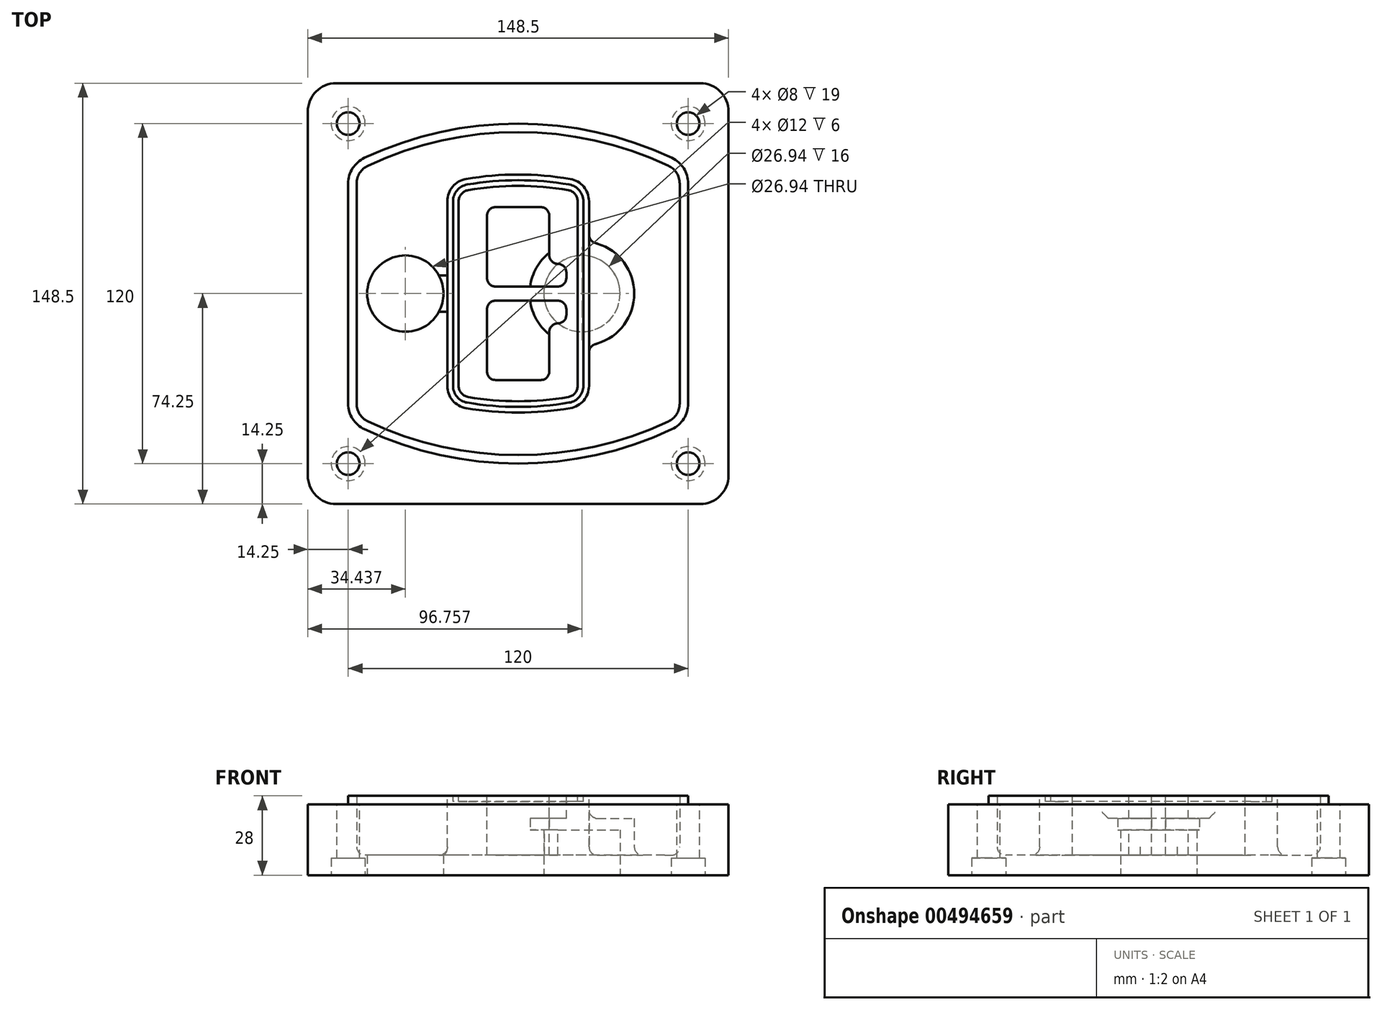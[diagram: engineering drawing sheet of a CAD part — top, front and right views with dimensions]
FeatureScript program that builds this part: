
annotation { "Feature Type Name" : "Feature", "Feature Type Description" : "" }
export const myFeature = defineFeature(function(context is Context, id is Id, definition is map)
    precondition{}
    {
        {
            var Q0;
            Q0=qCreatedBy(makeId("Top.planeOp"),FACE);
            var sketch = newSketch(context, id + "F0", { "sketchPlane" : qUnion([Q0])});
            skPoint(sketch, "E0.rect.middle", {"position": v(0, 0) * mm});
            skLineSegment(sketch, "E1.bottom", {"start": v(-64.25, -74.25) * mm, "end": v(64.25, -74.25) * mm});
            skLineSegment(sketch, "E1.top", {"start": v(-64.25, 74.25) * mm, "end": v(64.25, 74.25) * mm});
            skLineSegment(sketch, "E1.left", {"start": v(-74.25, -64.25) * mm, "end": v(-74.25, 64.25) * mm});
            skLineSegment(sketch, "E1.right", {"start": v(74.25, -64.25) * mm, "end": v(74.25, 64.25) * mm});
            skLineSegment(sketch, "E2", {"start": v(-74.25, 74.25) * mm, "end": v(74.25, -74.25) * mm, "construction": true});
            skLineSegment(sketch, "E3", {"start": v(74.25, 74.25) * mm, "end": v(-74.25, -74.25) * mm, "construction": true});
            skCircle(sketch, "E4", {"center": v(-60, 60) * mm, "radius": 4 * mm});
            skCircle(sketch, "E5", {"center": v(60, 60) * mm, "radius": 4 * mm});
            skCircle(sketch, "E6", {"center": v(60, -60) * mm, "radius": 4 * mm});
            skCircle(sketch, "E7", {"center": v(-60, -60) * mm, "radius": 4 * mm});
            skLineSegment(sketch, "E8", {"start": v(-60, 60) * mm, "end": v(60, 60) * mm, "construction": true});
            skLineSegment(sketch, "E9", {"start": v(60, 60) * mm, "end": v(60, -60) * mm, "construction": true});
            skLineSegment(sketch, "E10", {"start": v(60, -60) * mm, "end": v(-60, -60) * mm, "construction": true});
            skLineSegment(sketch, "E11", {"start": v(-60, -60) * mm, "end": v(-60, 60) * mm, "construction": true});
            skLineSegment(sketch, "E12", {"start": v(-60, 38.83) * mm, "end": v(-60, -38.83) * mm});
            skLineSegment(sketch, "E13", {"start": v(60, 38.83) * mm, "end": v(60, -38.83) * mm});
            skArc(sketch, "E14", {"start": v(54.26, 47.88) * mm, "mid": v(0, 60) * mm, "end": v(-54.26, 47.88) * mm});
            skArc(sketch, "E15", {"start": v(-54.26, -47.88) * mm, "mid": v(0, -60) * mm, "end": v(54.26, -47.88) * mm});
            skLineSegment(sketch, "E16", {"start": v(-60, 0) * mm, "end": v(60, 0) * mm, "construction": true});
            skPoint(sketch, "E17.visualSharp", {"position": v(-60, -45) * mm});
            skArc(sketch, "E17.filletArc", {"start": v(-60, -38.83) * mm, "mid": v(-58.44, -44.2) * mm, "end": v(-54.26, -47.88) * mm});
            skPoint(sketch, "E18.visualSharp", {"position": v(-60, 45) * mm});
            skArc(sketch, "E18.filletArc", {"start": v(-54.26, 47.88) * mm, "mid": v(-58.44, 44.2) * mm, "end": v(-60, 38.83) * mm});
            skPoint(sketch, "E19.visualSharp", {"position": v(60, 45) * mm});
            skArc(sketch, "E19.filletArc", {"start": v(60, 38.83) * mm, "mid": v(58.44, 44.2) * mm, "end": v(54.26, 47.88) * mm});
            skPoint(sketch, "E20.visualSharp", {"position": v(60, -45) * mm});
            skArc(sketch, "E20.filletArc", {"start": v(54.26, -47.88) * mm, "mid": v(58.44, -44.2) * mm, "end": v(60, -38.83) * mm});
            skPoint(sketch, "E21.visualSharp", {"position": v(-74.25, 74.25) * mm});
            skArc(sketch, "E21.filletArc", {"start": v(-64.25, 74.25) * mm, "mid": v(-71.32, 71.32) * mm, "end": v(-74.25, 64.25) * mm});
            skPoint(sketch, "E22.visualSharp", {"position": v(74.25, 74.25) * mm});
            skArc(sketch, "E22.filletArc", {"start": v(74.25, 64.25) * mm, "mid": v(71.32, 71.32) * mm, "end": v(64.25, 74.25) * mm});
            skPoint(sketch, "E23.visualSharp", {"position": v(74.25, -74.25) * mm});
            skArc(sketch, "E23.filletArc", {"start": v(64.25, -74.25) * mm, "mid": v(71.32, -71.32) * mm, "end": v(74.25, -64.25) * mm});
            skPoint(sketch, "E24.visualSharp", {"position": v(-74.25, -74.25) * mm});
            skArc(sketch, "E24.filletArc", {"start": v(-74.25, -64.25) * mm, "mid": v(-71.32, -71.32) * mm, "end": v(-64.25, -74.25) * mm});
            skArc(sketch, "E25.0", {"start": v(57, 38.83) * mm, "mid": v(55.9, 42.58) * mm, "end": v(52.98, 45.17) * mm});
            skLineSegment(sketch, "E25.1", {"start": v(57, 38.83) * mm, "end": v(57, -38.83) * mm});
            skArc(sketch, "E25.2", {"start": v(52.98, -45.17) * mm, "mid": v(55.9, -42.58) * mm, "end": v(57, -38.83) * mm});
            skArc(sketch, "E25.3", {"start": v(-52.98, -45.17) * mm, "mid": v(0, -57) * mm, "end": v(52.98, -45.17) * mm});
            skArc(sketch, "E25.4", {"start": v(-57, -38.83) * mm, "mid": v(-55.9, -42.58) * mm, "end": v(-52.98, -45.17) * mm});
            skArc(sketch, "E25.5", {"start": v(52.98, 45.17) * mm, "mid": v(0, 57) * mm, "end": v(-52.98, 45.17) * mm});
            skLineSegment(sketch, "E25.6", {"start": v(-57, 38.83) * mm, "end": v(-57, -38.83) * mm});
            skArc(sketch, "E25.7", {"start": v(-52.98, 45.17) * mm, "mid": v(-55.9, 42.58) * mm, "end": v(-57, 38.83) * mm});
            skArc(sketch, "E26.0", {"start": v(-55.96, 51.5) * mm, "mid": v(-61.82, 46.33) * mm, "end": v(-64, 38.83) * mm});
            skArc(sketch, "E26.1", {"start": v(55.96, 51.5) * mm, "mid": v(0, 64) * mm, "end": v(-55.96, 51.5) * mm});
            skArc(sketch, "E26.2", {"start": v(64, 38.83) * mm, "mid": v(61.82, 46.33) * mm, "end": v(55.96, 51.5) * mm});
            skLineSegment(sketch, "E26.3", {"start": v(64, 38.83) * mm, "end": v(64, -38.83) * mm});
            skArc(sketch, "E26.4", {"start": v(55.96, -51.5) * mm, "mid": v(61.82, -46.33) * mm, "end": v(64, -38.83) * mm});
            skLineSegment(sketch, "E26.5", {"start": v(-64, 38.83) * mm, "end": v(-64, -38.83) * mm});
            skArc(sketch, "E26.6", {"start": v(-55.96, -51.5) * mm, "mid": v(0, -64) * mm, "end": v(55.96, -51.5) * mm});
            skArc(sketch, "E26.7", {"start": v(-64, -38.83) * mm, "mid": v(-61.82, -46.33) * mm, "end": v(-55.96, -51.5) * mm});
            skSolve(sketch);
        }
        {
            var Q0;
            Q0=makeQuery(id+"F0.imprint","IMPRINT",FACE,{"disambiguationData":[TD([[makeQuery(id+"F0.imprint","IMPRINT",EDGE,{"derivedFrom":sQuery(id+"F0.wireOp",EDGE,"E1.bottom")}),1.0]])]});
            var Q1;
            Q1=makeQuery(id+"F0.imprint","IMPRINT",FACE,{"disambiguationData":[TD([[makeQuery(id+"F0.imprint","IMPRINT",EDGE,{"derivedFrom":sQuery(id+"F0.wireOp",EDGE,"E12")}),1.0]])]});
            var Q2;
            Q2=makeQuery(id+"F0.imprint","IMPRINT",FACE,{"disambiguationData":[TD([[makeQuery(id+"F0.imprint","IMPRINT",EDGE,{"derivedFrom":sQuery(id+"F0.wireOp",EDGE,"E25.0")}),1.0]])]});
            var Q3;
            Q3=makeQuery(id+"F0.imprint","IMPRINT",FACE,{"disambiguationData":[TD([[makeQuery(id+"F0.imprint","IMPRINT",EDGE,{"derivedFrom":sQuery(id+"F0.wireOp",EDGE,"E12")}),-1.0]])]});
            extrude(context, id + "F1", {"entities" : qUnion([Q0, Q1, Q2, Q3]), "oppositeDirection" : true, "depth" : 25 * mm});
        }
        {
            var Q0;
            Q0=makeQuery(id+"F0.imprint","IMPRINT",FACE,{"disambiguationData":[TD([[makeQuery(id+"F0.imprint","IMPRINT",EDGE,{"derivedFrom":sQuery(id+"F0.wireOp",EDGE,"E12")}),1.0]])]});
            extrude(context, id + "F2", {"entities" : qUnion([Q0]), "operationType" : NewBodyOperationType.ADD, "depth" : 3 * mm});
        }
        {
            var Q0;
            Q0=makeQuery(id+"F0.imprint","IMPRINT",FACE,{"disambiguationData":[TD([[makeQuery(id+"F0.imprint","IMPRINT",EDGE,{"derivedFrom":sQuery(id+"F0.wireOp",EDGE,"E25.0")}),1.0]])]});
            extrude(context, id + "F3", {"entities" : qUnion([Q0]), "operationType" : NewBodyOperationType.REMOVE, "oppositeDirection" : true, "depth" : 18 * mm});
        }
        {
            var Q0;
            Q0=makeQuery(id+"F2.opExtrude","CAP_FACE",FACE,{"disambiguationData":[OSD([sQuery(id+"F0.wireOp",EDGE,"E12"),sQuery(id+"F0.wireOp",EDGE,"E13"),sQuery(id+"F0.wireOp",EDGE,"E14"),sQuery(id+"F0.wireOp",EDGE,"E15"),sQuery(id+"F0.wireOp",EDGE,"E17.filletArc"),sQuery(id+"F0.wireOp",EDGE,"E18.filletArc"),sQuery(id+"F0.wireOp",EDGE,"E19.filletArc"),sQuery(id+"F0.wireOp",EDGE,"E20.filletArc"),sQuery(id+"F0.wireOp",EDGE,"E25.0"),sQuery(id+"F0.wireOp",EDGE,"E25.1"),sQuery(id+"F0.wireOp",EDGE,"E25.2"),sQuery(id+"F0.wireOp",EDGE,"E25.3"),sQuery(id+"F0.wireOp",EDGE,"E25.4"),sQuery(id+"F0.wireOp",EDGE,"E25.5"),sQuery(id+"F0.wireOp",EDGE,"E25.6"),sQuery(id+"F0.wireOp",EDGE,"E25.7")])],"isStart":false});
            var sketch = newSketch(context, id + "F4", { "sketchPlane" : qUnion([Q0])});
            skArc(sketch, "E27.0", {"start": v(-18.34, -40.45) * mm, "mid": v(0, -42) * mm, "end": v(18.34, -40.45) * mm});
            skArc(sketch, "E28.0", {"start": v(18.34, 40.45) * mm, "mid": v(0, 42) * mm, "end": v(-18.34, 40.45) * mm});
            skLineSegment(sketch, "E29", {"start": v(-25, 32.57) * mm, "end": v(-25, -32.57) * mm});
            skLineSegment(sketch, "E30", {"start": v(25, 32.57) * mm, "end": v(25, -32.57) * mm});
            skLineSegment(sketch, "E31", {"start": v(-25, 39.1) * mm, "end": v(25, 39.1) * mm, "construction": true});
            skLineSegment(sketch, "E32", {"start": v(-25, -39.1) * mm, "end": v(25, -39.1) * mm, "construction": true});
            skPoint(sketch, "E33.visualSharp", {"position": v(-25, 39.1) * mm});
            skArc(sketch, "E33.filletArc", {"start": v(-18.34, 40.45) * mm, "mid": v(-23.11, 37.73) * mm, "end": v(-25, 32.57) * mm});
            skPoint(sketch, "E34.visualSharp", {"position": v(25, 39.1) * mm});
            skArc(sketch, "E34.filletArc", {"start": v(25, 32.57) * mm, "mid": v(23.11, 37.73) * mm, "end": v(18.34, 40.45) * mm});
            skPoint(sketch, "E35.visualSharp", {"position": v(25, -39.1) * mm});
            skArc(sketch, "E35.filletArc", {"start": v(18.34, -40.45) * mm, "mid": v(23.11, -37.73) * mm, "end": v(25, -32.57) * mm});
            skPoint(sketch, "E36.visualSharp", {"position": v(-25, -39.1) * mm});
            skArc(sketch, "E36.filletArc", {"start": v(-25, -32.57) * mm, "mid": v(-23.11, -37.73) * mm, "end": v(-18.34, -40.45) * mm});
            skArc(sketch, "E37.0", {"start": v(52.98, 45.17) * mm, "mid": v(0, 57) * mm, "end": v(-52.98, 45.17) * mm});
            skArc(sketch, "E37.1", {"start": v(-52.98, 45.17) * mm, "mid": v(-55.9, 42.58) * mm, "end": v(-57, 38.83) * mm});
            skLineSegment(sketch, "E37.2", {"start": v(-57, 38.83) * mm, "end": v(-57, -38.83) * mm});
            skArc(sketch, "E37.3", {"start": v(-57, -38.83) * mm, "mid": v(-55.9, -42.58) * mm, "end": v(-52.98, -45.17) * mm});
            skArc(sketch, "E37.4", {"start": v(-52.98, -45.17) * mm, "mid": v(0, -57) * mm, "end": v(52.98, -45.17) * mm});
            skArc(sketch, "E37.5", {"start": v(52.98, -45.17) * mm, "mid": v(55.9, -42.58) * mm, "end": v(57, -38.83) * mm});
            skLineSegment(sketch, "E37.6", {"start": v(57, 38.83) * mm, "end": v(57, -38.83) * mm});
            skArc(sketch, "E37.7", {"start": v(57, 38.83) * mm, "mid": v(55.9, 42.58) * mm, "end": v(52.98, 45.17) * mm});
            skLineSegment(sketch, "E38.0", {"start": v(23, 32.57) * mm, "end": v(23, -32.57) * mm});
            skArc(sketch, "E38.1", {"start": v(18, -38.48) * mm, "mid": v(21.58, -36.44) * mm, "end": v(23, -32.57) * mm});
            skArc(sketch, "E38.2", {"start": v(-18, -38.48) * mm, "mid": v(0, -40) * mm, "end": v(18, -38.48) * mm});
            skArc(sketch, "E38.3", {"start": v(-23, -32.57) * mm, "mid": v(-21.58, -36.44) * mm, "end": v(-18, -38.48) * mm});
            skLineSegment(sketch, "E38.4", {"start": v(-23, 32.57) * mm, "end": v(-23, -32.57) * mm});
            skArc(sketch, "E38.5", {"start": v(23, 32.57) * mm, "mid": v(21.58, 36.44) * mm, "end": v(18, 38.48) * mm});
            skArc(sketch, "E38.6", {"start": v(-18, 38.48) * mm, "mid": v(-21.58, 36.44) * mm, "end": v(-23, 32.57) * mm});
            skArc(sketch, "E38.7", {"start": v(18, 38.48) * mm, "mid": v(0, 40) * mm, "end": v(-18, 38.48) * mm});
            skArc(sketch, "E39.0", {"start": v(21, 32.57) * mm, "mid": v(20.06, 35.15) * mm, "end": v(17.67, 36.5) * mm});
            skLineSegment(sketch, "E39.1", {"start": v(21, 32.57) * mm, "end": v(21, -32.57) * mm});
            skArc(sketch, "E39.2", {"start": v(17.67, -36.5) * mm, "mid": v(20.06, -35.15) * mm, "end": v(21, -32.57) * mm});
            skArc(sketch, "E39.3", {"start": v(-17.67, -36.5) * mm, "mid": v(0, -38) * mm, "end": v(17.67, -36.5) * mm});
            skArc(sketch, "E39.4", {"start": v(-21, -32.57) * mm, "mid": v(-20.06, -35.15) * mm, "end": v(-17.67, -36.5) * mm});
            skArc(sketch, "E39.5", {"start": v(17.67, 36.5) * mm, "mid": v(0, 38) * mm, "end": v(-17.67, 36.5) * mm});
            skLineSegment(sketch, "E39.6", {"start": v(-21, 32.57) * mm, "end": v(-21, -32.57) * mm});
            skArc(sketch, "E39.7", {"start": v(-17.67, 36.5) * mm, "mid": v(-20.06, 35.15) * mm, "end": v(-21, 32.57) * mm});
            skLineSegment(sketch, "E40", {"start": v(-25, 0) * mm, "end": v(25, 0) * mm, "construction": true});
            skLineSegment(sketch, "E41", {"start": v(-11, 5.5) * mm, "end": v(-11, 27.5) * mm});
            skLineSegment(sketch, "E42", {"start": v(-8, 30.5) * mm, "end": v(8, 30.5) * mm});
            skLineSegment(sketch, "E43", {"start": v(11, 27.5) * mm, "end": v(11, 13.5) * mm});
            skLineSegment(sketch, "E44", {"start": v(14, 10.5) * mm, "end": v(14, 10.5) * mm});
            skLineSegment(sketch, "E45", {"start": v(17, 7.5) * mm, "end": v(17, 5.5) * mm});
            skLineSegment(sketch, "E46", {"start": v(14, 2.5) * mm, "end": v(-8, 2.5) * mm});
            skPoint(sketch, "E47.visualSharp", {"position": v(-11, 30.5) * mm});
            skArc(sketch, "E47.filletArc", {"start": v(-8, 30.5) * mm, "mid": v(-10.12, 29.62) * mm, "end": v(-11, 27.5) * mm});
            skPoint(sketch, "E48.visualSharp", {"position": v(11, 30.5) * mm});
            skArc(sketch, "E48.filletArc", {"start": v(11, 27.5) * mm, "mid": v(10.12, 29.62) * mm, "end": v(8, 30.5) * mm});
            skPoint(sketch, "E49.visualSharp", {"position": v(11, 10.5) * mm});
            skArc(sketch, "E49.filletArc", {"start": v(11, 13.5) * mm, "mid": v(11.88, 11.38) * mm, "end": v(14, 10.5) * mm});
            skPoint(sketch, "E50.visualSharp", {"position": v(17, 10.5) * mm});
            skArc(sketch, "E50.filletArc", {"start": v(17, 7.5) * mm, "mid": v(16.12, 9.62) * mm, "end": v(14, 10.5) * mm});
            skPoint(sketch, "E51.visualSharp", {"position": v(17, 2.5) * mm});
            skArc(sketch, "E51.filletArc", {"start": v(14, 2.5) * mm, "mid": v(16.12, 3.38) * mm, "end": v(17, 5.5) * mm});
            skPoint(sketch, "E52.visualSharp", {"position": v(-11, 2.5) * mm});
            skArc(sketch, "E52.filletArc", {"start": v(-11, 5.5) * mm, "mid": v(-10.12, 3.38) * mm, "end": v(-8, 2.5) * mm});
            skLineSegment(sketch, "E53.0.MirrorCS", {"start": v(14, -2.5) * mm, "end": v(-8, -2.5) * mm});
            skArc(sketch, "E54.0.MirrorCS", {"start": v(-11, -5.5) * mm, "mid": v(-10.12, -3.38) * mm, "end": v(-8, -2.5) * mm});
            skLineSegment(sketch, "E55.0.MirrorCS", {"start": v(-11, -5.5) * mm, "end": v(-11, -27.5) * mm});
            skArc(sketch, "E56.0.MirrorCS", {"start": v(-8, -30.5) * mm, "mid": v(-10.12, -29.62) * mm, "end": v(-11, -27.5) * mm});
            skLineSegment(sketch, "E57.0.MirrorCS", {"start": v(-8, -30.5) * mm, "end": v(8, -30.5) * mm});
            skArc(sketch, "E58.0.MirrorCS", {"start": v(11, -27.5) * mm, "mid": v(10.12, -29.62) * mm, "end": v(8, -30.5) * mm});
            skLineSegment(sketch, "E59.0.MirrorCS", {"start": v(11, -27.5) * mm, "end": v(11, -13.5) * mm});
            skArc(sketch, "E60.0.MirrorCS", {"start": v(11, -13.5) * mm, "mid": v(11.88, -11.38) * mm, "end": v(14, -10.5) * mm});
            skArc(sketch, "E61.0.MirrorCS", {"start": v(17, -7.5) * mm, "mid": v(16.12, -9.62) * mm, "end": v(14, -10.5) * mm});
            skLineSegment(sketch, "E62.0.MirrorCS", {"start": v(17, -7.5) * mm, "end": v(17, -5.5) * mm});
            skArc(sketch, "E63.0.MirrorCS", {"start": v(14, -2.5) * mm, "mid": v(16.12, -3.38) * mm, "end": v(17, -5.5) * mm});
            skSolve(sketch);
        }
        {
            var Q0;
            Q0=makeQuery(id+"F4.imprint","IMPRINT",FACE,{"disambiguationData":[TD([[makeQuery(id+"F4.imprint","IMPRINT",EDGE,{"derivedFrom":sQuery(id+"F4.wireOp",EDGE,"E27.0")}),1.0]])]});
            var Q1;
            Q1=makeQuery(id+"F4.imprint","IMPRINT",FACE,{"disambiguationData":[TD([[makeQuery(id+"F4.imprint","IMPRINT",EDGE,{"derivedFrom":sQuery(id+"F4.wireOp",EDGE,"E38.0")}),-1.0]])]});
            var Q2;
            Q2=makeQuery(id+"F4.imprint","IMPRINT",FACE,{"disambiguationData":[TD([[makeQuery(id+"F4.imprint","IMPRINT",EDGE,{"derivedFrom":sQuery(id+"F4.wireOp",EDGE,"E39.0")}),1.0]])]});
            extrude(context, id + "F5", {"entities" : qUnion([Q0, Q1, Q2]), "operationType" : NewBodyOperationType.ADD, "endBound" : BoundingType.UP_TO_NEXT, "oppositeDirection" : true, "depth" : 25 * mm});
        }
        {
            var Q0;
            Q0=makeQuery(id+"F4.imprint","IMPRINT",FACE,{"disambiguationData":[TD([[makeQuery(id+"F4.imprint","IMPRINT",EDGE,{"derivedFrom":sQuery(id+"F4.wireOp",EDGE,"E38.0")}),-1.0]])]});
            extrude(context, id + "F6", {"entities" : qUnion([Q0]), "operationType" : NewBodyOperationType.REMOVE, "oppositeDirection" : true, "depth" : 2 * mm});
        }
        {
            var Q0;
            Q0=makeQuery(id+"F1.opExtrude","CAP_FACE",FACE,{"disambiguationData":[OSD([sQuery(id+"F0.wireOp",EDGE,"E1.bottom"),sQuery(id+"F0.wireOp",EDGE,"E1.top"),sQuery(id+"F0.wireOp",EDGE,"E1.left"),sQuery(id+"F0.wireOp",EDGE,"E1.right"),sQuery(id+"F0.wireOp",EDGE,"E4"),sQuery(id+"F0.wireOp",EDGE,"E5"),sQuery(id+"F0.wireOp",EDGE,"E6"),sQuery(id+"F0.wireOp",EDGE,"E7"),sQuery(id+"F0.wireOp",EDGE,"E21.filletArc"),sQuery(id+"F0.wireOp",EDGE,"E22.filletArc"),sQuery(id+"F0.wireOp",EDGE,"E23.filletArc"),sQuery(id+"F0.wireOp",EDGE,"E24.filletArc")])],"isStart":false});
            var sketch = newSketch(context, id + "F7", { "sketchPlane" : qUnion([Q0])});
            skCircle(sketch, "E64", {"center": v(22.5, 0) * mm, "radius": 13.47 * mm});
            skCircle(sketch, "E65", {"center": v(-39.81, 0) * mm, "radius": 13.47 * mm});
            skLineSegment(sketch, "E66", {"start": v(74.25, 0) * mm, "end": v(-74.25, 0) * mm});
            skCircle(sketch, "E67", {"center": v(22.5, 0) * mm, "radius": 18.47 * mm});
            skCircle(sketch, "E68", {"center": v(60, -60) * mm, "radius": 6 * mm});
            skCircle(sketch, "E69", {"center": v(-60, -60) * mm, "radius": 6 * mm});
            skCircle(sketch, "E70", {"center": v(-60, 60) * mm, "radius": 6 * mm});
            skCircle(sketch, "E71", {"center": v(60, 60) * mm, "radius": 6 * mm});
            skSolve(sketch);
        }
        {
            var Q0;
            {var subQ1=sQuery(id+"F7.wireOp",EDGE,"E66");var subQ4=sQuery(id+"F7.wireOp",EDGE,"E64");var subQ6=makeQuery(id+"F7.imprint","INTERSECT",VERTEX,{"disambiguationData":[OD(0.0)],"derivedFrom":[subQ4,subQ1]});Q0=makeQuery(id+"F7.imprint","IMPRINT",FACE,{"disambiguationData":[TD([[makeQuery(id+"F7.imprint","IMPRINT",EDGE,{"disambiguationData":[TD([[subQ6,-1.0]])],"derivedFrom":subQ4}),-1.0]])]});}
            var Q1;
            {var subQ0=sQuery(id+"F7.wireOp",EDGE,"E66");var subQ1=sQuery(id+"F7.wireOp",EDGE,"E64");var subQ3=makeQuery(id+"F7.imprint","INTERSECT",VERTEX,{"disambiguationData":[OD(0.0)],"derivedFrom":[subQ1,subQ0]});Q1=makeQuery(id+"F7.imprint","IMPRINT",FACE,{"disambiguationData":[TD([[makeQuery(id+"F7.imprint","IMPRINT",EDGE,{"disambiguationData":[TD([[subQ3,-1.0]])],"derivedFrom":subQ1}),1.0]])]});}
            var Q2;
            {var subQ0=sQuery(id+"F7.wireOp",EDGE,"E66");var subQ1=sQuery(id+"F7.wireOp",EDGE,"E64");var subQ3=makeQuery(id+"F7.imprint","INTERSECT",VERTEX,{"disambiguationData":[OD(0.0)],"derivedFrom":[subQ1,subQ0]});Q2=makeQuery(id+"F7.imprint","IMPRINT",FACE,{"disambiguationData":[TD([[makeQuery(id+"F7.imprint","IMPRINT",EDGE,{"disambiguationData":[TD([[subQ3,1.0]])],"derivedFrom":subQ1}),1.0]])]});}
            var Q3;
            {var subQ1=sQuery(id+"F7.wireOp",EDGE,"E66");var subQ4=sQuery(id+"F7.wireOp",EDGE,"E64");var subQ6=makeQuery(id+"F7.imprint","INTERSECT",VERTEX,{"disambiguationData":[OD(0.0)],"derivedFrom":[subQ4,subQ1]});Q3=makeQuery(id+"F7.imprint","IMPRINT",FACE,{"disambiguationData":[TD([[makeQuery(id+"F7.imprint","IMPRINT",EDGE,{"disambiguationData":[TD([[subQ6,1.0]])],"derivedFrom":subQ4}),-1.0]])]});}
            extrude(context, id + "F8", {"entities" : qUnion([Q0, Q1, Q2, Q3]), "operationType" : NewBodyOperationType.ADD, "oppositeDirection" : true, "depth" : 20 * mm});
        }
        {
            var Q0;
            {var subQ0=sQuery(id+"F7.wireOp",EDGE,"E66");var subQ1=sQuery(id+"F7.wireOp",EDGE,"E64");var subQ3=makeQuery(id+"F7.imprint","INTERSECT",VERTEX,{"disambiguationData":[OD(0.0)],"derivedFrom":[subQ1,subQ0]});Q0=makeQuery(id+"F7.imprint","IMPRINT",FACE,{"disambiguationData":[TD([[makeQuery(id+"F7.imprint","IMPRINT",EDGE,{"disambiguationData":[TD([[subQ3,-1.0]])],"derivedFrom":subQ1}),1.0]])]});}
            var Q1;
            {var subQ0=sQuery(id+"F7.wireOp",EDGE,"E66");var subQ1=sQuery(id+"F7.wireOp",EDGE,"E64");var subQ3=makeQuery(id+"F7.imprint","INTERSECT",VERTEX,{"disambiguationData":[OD(0.0)],"derivedFrom":[subQ1,subQ0]});Q1=makeQuery(id+"F7.imprint","IMPRINT",FACE,{"disambiguationData":[TD([[makeQuery(id+"F7.imprint","IMPRINT",EDGE,{"disambiguationData":[TD([[subQ3,1.0]])],"derivedFrom":subQ1}),1.0]])]});}
            extrude(context, id + "F9", {"entities" : qUnion([Q0, Q1]), "operationType" : NewBodyOperationType.REMOVE, "oppositeDirection" : true, "depth" : 16 * mm});
        }
        {
            var Q0;
            {var subQ0=sQuery(id+"F7.wireOp",EDGE,"E66");var subQ1=sQuery(id+"F7.wireOp",EDGE,"E65");var subQ3=makeQuery(id+"F7.imprint","INTERSECT",VERTEX,{"disambiguationData":[OD(0.0)],"derivedFrom":[subQ1,subQ0]});Q0=makeQuery(id+"F7.imprint","IMPRINT",FACE,{"disambiguationData":[TD([[makeQuery(id+"F7.imprint","IMPRINT",EDGE,{"disambiguationData":[TD([[subQ3,-1.0]])],"derivedFrom":subQ1}),1.0]])]});}
            var Q1;
            {var subQ0=sQuery(id+"F7.wireOp",EDGE,"E66");var subQ1=sQuery(id+"F7.wireOp",EDGE,"E65");var subQ3=makeQuery(id+"F7.imprint","INTERSECT",VERTEX,{"disambiguationData":[OD(0.0)],"derivedFrom":[subQ1,subQ0]});Q1=makeQuery(id+"F7.imprint","IMPRINT",FACE,{"disambiguationData":[TD([[makeQuery(id+"F7.imprint","IMPRINT",EDGE,{"disambiguationData":[TD([[subQ3,1.0]])],"derivedFrom":subQ1}),1.0]])]});}
            extrude(context, id + "F10", {"entities" : qUnion([Q0, Q1]), "operationType" : NewBodyOperationType.REMOVE, "oppositeDirection" : true, "depth" : 25 * mm});
        }
        {
            var Q0;
            Q0=makeQuery(id+"F7.imprint","IMPRINT",FACE,{"disambiguationData":[TD([[makeQuery(id+"F7.imprint","IMPRINT",EDGE,{"derivedFrom":sQuery(id+"F7.wireOp",EDGE,"E68")}),1.0]])]});
            var Q1;
            Q1=makeQuery(id+"F7.imprint","IMPRINT",FACE,{"disambiguationData":[TD([[makeQuery(id+"F7.imprint","IMPRINT",EDGE,{"derivedFrom":makeQuery(id+"F1.opExtrude","CAP_EDGE",EDGE,{"disambiguationData":[OSD([sQuery(id+"F0.wireOp",EDGE,"E5")])],"isStart":false})}),-1.0]])]});
            var Q2;
            Q2=makeQuery(id+"F7.imprint","IMPRINT",FACE,{"disambiguationData":[TD([[makeQuery(id+"F7.imprint","IMPRINT",EDGE,{"derivedFrom":sQuery(id+"F7.wireOp",EDGE,"E69")}),1.0]])]});
            var Q3;
            Q3=makeQuery(id+"F7.imprint","IMPRINT",FACE,{"disambiguationData":[TD([[makeQuery(id+"F7.imprint","IMPRINT",EDGE,{"derivedFrom":makeQuery(id+"F1.opExtrude","CAP_EDGE",EDGE,{"disambiguationData":[OSD([sQuery(id+"F0.wireOp",EDGE,"E4")])],"isStart":false})}),-1.0]])]});
            var Q4;
            Q4=makeQuery(id+"F7.imprint","IMPRINT",FACE,{"disambiguationData":[TD([[makeQuery(id+"F7.imprint","IMPRINT",EDGE,{"derivedFrom":sQuery(id+"F7.wireOp",EDGE,"E70")}),1.0]])]});
            var Q5;
            Q5=makeQuery(id+"F7.imprint","IMPRINT",FACE,{"disambiguationData":[TD([[makeQuery(id+"F7.imprint","IMPRINT",EDGE,{"derivedFrom":makeQuery(id+"F1.opExtrude","CAP_EDGE",EDGE,{"disambiguationData":[OSD([sQuery(id+"F0.wireOp",EDGE,"E7")])],"isStart":false})}),-1.0]])]});
            var Q6;
            Q6=makeQuery(id+"F7.imprint","IMPRINT",FACE,{"disambiguationData":[TD([[makeQuery(id+"F7.imprint","IMPRINT",EDGE,{"derivedFrom":sQuery(id+"F7.wireOp",EDGE,"E71")}),1.0]])]});
            var Q7;
            Q7=makeQuery(id+"F7.imprint","IMPRINT",FACE,{"disambiguationData":[TD([[makeQuery(id+"F7.imprint","IMPRINT",EDGE,{"derivedFrom":makeQuery(id+"F1.opExtrude","CAP_EDGE",EDGE,{"disambiguationData":[OSD([sQuery(id+"F0.wireOp",EDGE,"E6")])],"isStart":false})}),-1.0]])]});
            extrude(context, id + "F11", {"entities" : qUnion([Q0, Q1, Q2, Q3, Q4, Q5, Q6, Q7]), "operationType" : NewBodyOperationType.REMOVE, "oppositeDirection" : true, "depth" : 6 * mm});
        }
        {
            var Q0;
            Q0=makeQuery(id+"F9.boolean.opBoolean","COPY",FACE,{"derivedFrom":makeQuery(id+"F9.opExtrude","CAP_FACE",FACE,{"disambiguationData":[OSD([sQuery(id+"F7.wireOp",EDGE,"E64")])],"isStart":false})});
            var sketch = newSketch(context, id + "F12", { "sketchPlane" : qUnion([Q0])});
            skArc(sketch, "E72.0", {"start": v(11, 14.45) * mm, "mid": v(6.45, 9.13) * mm, "end": v(4.2, 2.5) * mm});
            skArc(sketch, "E72.1", {"start": v(4.2, -2.5) * mm, "mid": v(6.45, -9.13) * mm, "end": v(11, -14.45) * mm});
            skLineSegment(sketch, "E73", {"start": v(4.2, -2.5) * mm, "end": v(14, -2.5) * mm});
            skLineSegment(sketch, "E74.0", {"start": v(14, 2.5) * mm, "end": v(4.2, 2.5) * mm});
            skArc(sketch, "E74.1", {"start": v(14, 2.5) * mm, "mid": v(16.12, 3.38) * mm, "end": v(17, 5.5) * mm});
            skLineSegment(sketch, "E74.2", {"start": v(17, 7.5) * mm, "end": v(17, 5.5) * mm});
            skArc(sketch, "E74.3", {"start": v(17, 7.5) * mm, "mid": v(16.12, 9.62) * mm, "end": v(14, 10.5) * mm});
            skArc(sketch, "E74.4", {"start": v(11, 13.5) * mm, "mid": v(11.88, 11.38) * mm, "end": v(14, 10.5) * mm});
            skLineSegment(sketch, "E74.5", {"start": v(11, 14.45) * mm, "end": v(11, 13.5) * mm});
            skLineSegment(sketch, "E74.7", {"start": v(14, -2.5) * mm, "end": v(4.2, -2.5) * mm});
            skArc(sketch, "E74.8", {"start": v(14, -2.5) * mm, "mid": v(16.12, -3.38) * mm, "end": v(17, -5.5) * mm});
            skLineSegment(sketch, "E74.9", {"start": v(17, -7.5) * mm, "end": v(17, -5.5) * mm});
            skArc(sketch, "E74.10", {"start": v(17, -7.5) * mm, "mid": v(16.12, -9.62) * mm, "end": v(14, -10.5) * mm});
            skArc(sketch, "E74.11", {"start": v(11, -13.5) * mm, "mid": v(11.88, -11.38) * mm, "end": v(14, -10.5) * mm});
            skLineSegment(sketch, "E74.12", {"start": v(11, -14.45) * mm, "end": v(11, -13.5) * mm});
            skPoint(sketch, "E75.orphan", {"position": v(11, -27.5) * mm});
            skPoint(sketch, "E76.orphan", {"position": v(-8, -2.5) * mm});
            skPoint(sketch, "E77.orphan", {"position": v(-8, 2.5) * mm});
            skPoint(sketch, "E78.orphan", {"position": v(11, 27.5) * mm});
            skSolve(sketch);
        }
        {
            var Q0;
            {var subQ7=sQuery(id+"F12.wireOp",EDGE,"E72.0");var subQ14=sQuery(id+"F12.wireOp",EDGE,"E72.1");var subQ16=sQuery(id+"F12.wireOp",EDGE,"E74.1");var subQ18=sQuery(id+"F12.wireOp",EDGE,"E74.8");Q0=qUnion([makeQuery(id+"F12.imprint","IMPRINT",FACE,{"disambiguationData":[TD([[makeQuery(id+"F12.imprint","IMPRINT",EDGE,{"derivedFrom":subQ7}),1.0]])]}),makeQuery(id+"F12.imprint","IMPRINT",FACE,{"disambiguationData":[TD([[makeQuery(id+"F12.imprint","IMPRINT",EDGE,{"derivedFrom":subQ14}),1.0]])]}),makeQuery(id+"F12.imprint","IMPRINT",FACE,{"disambiguationData":[TD([[makeQuery(id+"F12.imprint","IMPRINT",EDGE,{"derivedFrom":subQ16}),1.0]])]}),makeQuery(id+"F12.imprint","IMPRINT",FACE,{"disambiguationData":[TD([[makeQuery(id+"F12.imprint","IMPRINT",EDGE,{"derivedFrom":subQ18}),-1.0]])]})]);}
            var Q1;
            Q1=makeQuery(id+"F5.boolean.opBoolean","SPLIT",FACE,{"disambiguationData":[TD([makeQuery(id+"F5.opExtrude","SWEPT_FACE",FACE,{"disambiguationData":[OSD([sQuery(id+"F4.wireOp",EDGE,"E41")])]})])],"derivedFrom":makeQuery(id+"F3.boolean.opBoolean","COPY",FACE,{"derivedFrom":makeQuery(id+"F3.opExtrude","CAP_FACE",FACE,{"disambiguationData":[OSD([sQuery(id+"F0.wireOp",EDGE,"E25.0"),sQuery(id+"F0.wireOp",EDGE,"E25.1"),sQuery(id+"F0.wireOp",EDGE,"E25.2"),sQuery(id+"F0.wireOp",EDGE,"E25.3"),sQuery(id+"F0.wireOp",EDGE,"E25.4"),sQuery(id+"F0.wireOp",EDGE,"E25.5"),sQuery(id+"F0.wireOp",EDGE,"E25.6"),sQuery(id+"F0.wireOp",EDGE,"E25.7")])],"isStart":false})})});
            extrude(context, id + "F13", {"entities" : qUnion([Q0]), "operationType" : NewBodyOperationType.REMOVE, "endBound" : BoundingType.UP_TO_SURFACE, "endBoundEntityFace" : qUnion([Q1]), "depth" : 25 * mm});
        }
        {
            var Q0;
            Q0=makeQuery(id+"F3.boolean.opBoolean","COPY",EDGE,{"derivedFrom":makeQuery(id+"F3.opExtrude","CAP_EDGE",EDGE,{"disambiguationData":[OSD([sQuery(id+"F0.wireOp",EDGE,"E25.6")])],"isStart":false})});
            var Q1;
            Q1=makeQuery(id+"F8.boolean.opBoolean","INTERSECT",EDGE,{"derivedFrom":[makeQuery(id+"F5.opExtrude","SWEPT_FACE",FACE,{"disambiguationData":[OSD([sQuery(id+"F4.wireOp",EDGE,"E30")])]}),makeQuery(id+"F8.opExtrude","CAP_FACE",FACE,{"disambiguationData":[OSD([sQuery(id+"F7.wireOp",EDGE,"E67")])],"isStart":false})]});
            var Q2;
            Q2=makeQuery(id+"F8.boolean.opBoolean","INTERSECT",EDGE,{"disambiguationData":[OD(1.0)],"derivedFrom":[makeQuery(id+"F5.opExtrude","SWEPT_FACE",FACE,{"disambiguationData":[OSD([sQuery(id+"F4.wireOp",EDGE,"E30")])]}),makeQuery(id+"F8.opExtrude","SWEPT_FACE",FACE,{"disambiguationData":[OSD([sQuery(id+"F7.wireOp",EDGE,"E67")])]})]});
            var Q3;
            {var subQ0=sQuery(id+"F4.wireOp",EDGE,"E30");Q3=makeQuery(id+"F8.boolean.opBoolean","SPLIT",EDGE,{"disambiguationData":[TD([makeQuery(id+"F5.opExtrude","SWEPT_FACE",FACE,{"disambiguationData":[OSD([sQuery(id+"F4.wireOp",EDGE,"E35.filletArc")])]})])],"derivedFrom":makeQuery(id+"F5.opExtrude","CAP_EDGE",EDGE,{"disambiguationData":[OSD([subQ0])],"isStart":false})});}
            var Q4;
            {var subQ0=sQuery(id+"F0.wireOp",EDGE,"E25.7");var subQ1=sQuery(id+"F0.wireOp",EDGE,"E25.1");var subQ2=sQuery(id+"F0.wireOp",EDGE,"E25.6");var subQ3=sQuery(id+"F0.wireOp",EDGE,"E25.5");var subQ4=sQuery(id+"F0.wireOp",EDGE,"E25.4");var subQ5=sQuery(id+"F0.wireOp",EDGE,"E25.0");var subQ6=sQuery(id+"F0.wireOp",EDGE,"E25.2");var subQ7=sQuery(id+"F0.wireOp",EDGE,"E25.3");Q4=makeQuery(id+"F8.boolean.opBoolean","INTERSECT",EDGE,{"derivedFrom":[makeQuery(id+"F5.boolean.opBoolean","SPLIT",FACE,{"disambiguationData":[TD([makeQuery(id+"F2.opExtrude","SWEPT_FACE",FACE,{"disambiguationData":[OSD([subQ5])]})])],"derivedFrom":makeQuery(id+"F3.boolean.opBoolean","COPY",FACE,{"derivedFrom":makeQuery(id+"F3.opExtrude","CAP_FACE",FACE,{"disambiguationData":[OSD([subQ5,subQ1,subQ6,subQ7,subQ4,subQ3,subQ2,subQ0])],"isStart":false})})}),makeQuery(id+"F8.opExtrude","SWEPT_FACE",FACE,{"disambiguationData":[OSD([sQuery(id+"F7.wireOp",EDGE,"E67")])]})]});}
            var Q5;
            Q5=makeQuery(id+"F8.boolean.opBoolean","INTERSECT",EDGE,{"disambiguationData":[OD(0.0)],"derivedFrom":[makeQuery(id+"F5.opExtrude","SWEPT_FACE",FACE,{"disambiguationData":[OSD([sQuery(id+"F4.wireOp",EDGE,"E30")])]}),makeQuery(id+"F8.opExtrude","SWEPT_FACE",FACE,{"disambiguationData":[OSD([sQuery(id+"F7.wireOp",EDGE,"E67")])]})]});
            fillet(context, id + "F14", {"entities" : qUnion([Q0, Q1, Q2, Q3, Q4, Q5]), "radius" : 3 * mm, "tangentPropagation" : true, "allowEdgeOverflow" : false});
        }
    });
